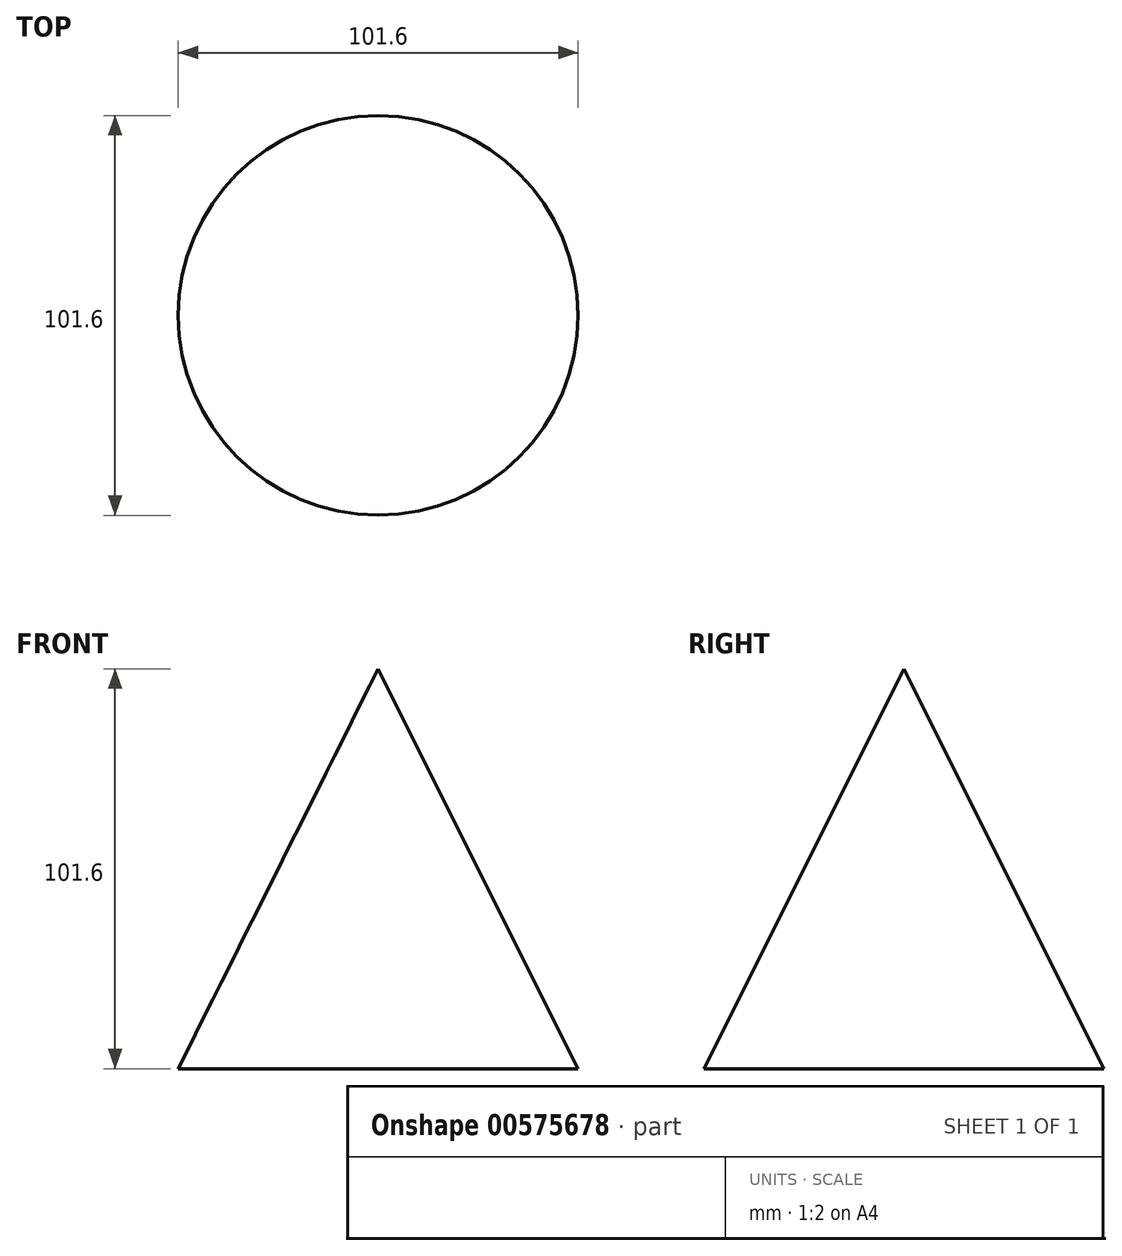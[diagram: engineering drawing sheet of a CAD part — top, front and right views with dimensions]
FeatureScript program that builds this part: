
annotation { "Feature Type Name" : "Feature", "Feature Type Description" : "" }
export const myFeature = defineFeature(function(context is Context, id is Id, definition is map)
    precondition{}
    {
        {
            var Q0;
            Q0=qCreatedBy(makeId("Front.planeOp"),FACE);
            var sketch = newSketch(context, id + "F0", { "sketchPlane" : qUnion([Q0])});
            skLineSegment(sketch, "E0", {"start": v(0, 0) * mm, "end": v(0, 101.6) * mm});
            skLineSegment(sketch, "E1", {"start": v(0, 101.6) * mm, "end": v(50.8, 0) * mm});
            skLineSegment(sketch, "E2", {"start": v(0, 0) * mm, "end": v(50.8, 0) * mm});
            skSolve(sketch);
        }
        {
            var Q0;
            Q0=makeQuery(id+"F0.imprint","IMPRINT",FACE,{"disambiguationData":[TD([[makeQuery(id+"F0.imprint","IMPRINT",EDGE,{"derivedFrom":sQuery(id+"F0.wireOp",EDGE,"E0")}),-1.0]])]});
            var Q1;
            Q1=sQuery(id+"F0.wireOp",EDGE,"E0");
            revolve(context, id + "F1", {"entities" : qUnion([Q0]), "axis" : qUnion([Q1]), "revolveType" : RevolveType.FULL});
        }
    });
